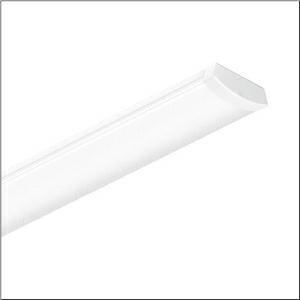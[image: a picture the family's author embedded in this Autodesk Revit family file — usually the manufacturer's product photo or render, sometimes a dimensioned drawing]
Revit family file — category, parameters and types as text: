
# Revit family: siluette_r__21_51ln12mdm20a_d267
name_source: partatom
category: Lighting Fixtures
units: mm (PartAtom-declared; Revit-internal decimal feet)

## family parameters
Cut with Voids When Loaded = No
Host = Face
Light Source = No
Part Type = Normal
Room Calculation Point = No
Round Connector Dimension = Use Diameter
Shared = No

## types (1)
- --- (1 x LED, 1510 lm, 12.2 W, 5000K)
    Apparent Load = 12 VA
    CIE Flux Codes = 43 73 92 94 100
    Color Rendering = 80
    Color Temperature = 5000K
    Default Elevation = 1800 mm
    Description = Siluette® 21, office luminaire, primary optical cover: enclosure, of PC, frosted, light emission: direct distribution, primary light characteristic: symmetric, installation type: suspended mounting, surface-mounted, LED, rated luminous flux: 2.630lm, luminous efficacy: 135lm/W, light colour: 830/840/850, colour temperature: 3000/4000/5000K, control gear: ON/OFF Multilumen, with terminal, 3-pole, mains connection: 220..240V, AC, 50/60Hz, rated input power: 20W, housing, of sheet steel, white, length: 600mm, width: 152mm, height: 53mm, end cap, of PMMA, white, protection rating (complete): IP44, insulation class (complete): insulation class I (protective earthing), certification: CE, UKCA, protection symbol: D, impact resistance: IK04, permissible operating ambient temperature: -20..+40°C, contact your sales advisor before using the luminaires in applications with unclear chemical exposure, large temperature fluctuations or condensation-forming humidity, corresponds to IFS (International Featured Standards) requirements for safety and quality in the food industry, packaging unit: 1 piece
    Height = 52 mm  [stored 0.170604 ft]
    Lamp = 1 x LED
    Lamp Light Flux = 1510 lm
    Lamp Power = 12.2 W
    Lamp count = 1
    Length = 645 mm
    Luminous efficacy = 124 lm/W
    Manufacturer = Siteco
    ModVariant = No
    Model = 51LN12MDM20A
    Mounting Place = Ceiling
    Mounting Type = Pendant
    Number of Poles = 1
    OnlyDefault = Yes
    Power Factor = 1
    Product Name = Siluette® 21
    Product group = office luminaire | ceiling pendant
    ProductGroupID = 904
    Protection Class = Protection class I
    Protection Degree = IP 44
    RLX_Detail_Level = 1
    RLX_Emergency_Light_Flux = 0 lm
    RLX_Emergency_Type = 0
    RLX_Emergency_Type_DB = No
    RlxData = <blob elided: 19177 chars, md5=1aa484a2>
    Socket = socket
    Standby Power = 0 W
    System Light Flux = 1510 lm
    System Power = 12 W
    Type Comments = individual setting: colour temperature 5000K, luminous flux: 58 % | (OFF | OFF | ON) | 200 mA
    Type Image = l_1296910.jpg
    URL = http://relux.com
    VarID = @adj_059450
    Voltage = 0 V
    Weight = 0.00 kg
    Width = 152 mm

note: [stored X ft] marks values corroborated as IEEE doubles in the binary element streams (Revit-internal decimal feet)

## geometry (parser evidence)
native form markers: Blend x4, Sweep x12
no freeform markers — native parametric forms only
